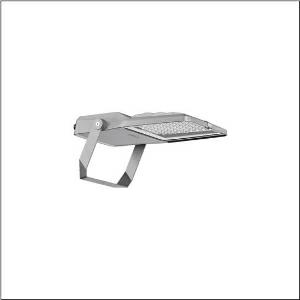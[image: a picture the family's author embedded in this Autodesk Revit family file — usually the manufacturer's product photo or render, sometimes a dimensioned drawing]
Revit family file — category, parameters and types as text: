
# Revit family: floodlight_fl_21_iq_mini___pl64_5xa7772d3e1a_da13
name_source: partatom
category: Lighting Fixtures
units: mm (PartAtom-declared; Revit-internal decimal feet)

## family parameters
Cut with Voids When Loaded = No
Host = Face
Light Source = No
Part Type = Normal
Room Calculation Point = No
Round Connector Dimension = Use Diameter
Shared = No

## types (1)
- --- (1 x LED, 14810 lm, 143 W, 3000K)
    Apparent Load = 143 VA
    CIE Flux Codes = 28 80 98 100 100
    Color Rendering = 80
    Color Temperature = 3000K
    Default Elevation = 1800 mm
    Description = Floodlight FL 21 iQ mini, floodlight, primary light control with lens, of PMMA, primary optical cover: protective disc, of toughened safety glass, transparent, light distribution: PL64, light emission: direct distribution, installation type: surface-mounted, LED, High Power LED, rated luminous flux: 14.810lm, luminous efficacy: 104lm/W, light colour: 830, colour temperature: 3000K, control gear: iQ Street-Remote/DALI, control: Street-Remote, Auto-Match, Temp-Guard, Night-Set, Smart-Wire, Desk-Remote (wireless, voltage-free reading and setting of iQ features in the workshop via application-optimized NFC function/RFID function), optimised constant luminous flux control (CLO 2.0), with terminal, 6-pole, mains connection: 220..240V, AC, 50/60Hz, start of lifetime: 143W, end of service life: 152W, reduction: 61W, luminaire housing, of diecast aluminium, powder-coated, Siteco® metallic grey (DB 702S), corrosivity category C5 mid according to DIN EN ISO 12944, suitable for swimming pools, chlorine-resistant, sealing non-destructively replaceable, mounting bracket, of steel, galvanised, powder-coated, Siteco® metallic grey (DB 702S), protection rating (complete): IP66, insulation class (complete): insulation class II (safety insulation), certification: CE, ENEC, VDE, protection symbol: D, impact resistance: IK08, permissible operating ambient temperature: -40..+40°C, permissible operating ambient temperature for outdoor applications: -40..+50°C, standard: DIN EN 12944, LABS conformity tested according to VDMA 24364:2018-05, packaging unit: 1 piece

Light Distribution: PL64
    Height = 70 mm
    Lamp = 1 x LED
    Lamp Light Flux = 14810 lm
    Lamp Power = 143 W
    Lamp count = 1
    Length = 485 mm
    Luminous efficacy = 104 lm/W
    Manufacturer = Siteco
    ModVariant = No
    Model = 5XA7772D3E1A
    Number of Poles = 1
    OnlyDefault = Yes
    Power Factor = 1
    Product Name = Floodlight FL 21 iQ mini | PL64
    Product group = floodlight | pylon annexe
    ProductGroupID = 6200
    Protection Class = Protection class II
    Protection Degree = IP 66
    RLX_Detail_Level = 1
    RLX_Emergency_Light_Flux = 0 lm
    RLX_Emergency_Type = 0
    RLX_Emergency_Type_DB = No
    RlxData = <blob elided: 96501 chars, md5=3e34074b>
    Socket = socket
    Standby Power = 0 W
    System Light Flux = 14810 lm
    System Power = 143 W
    Type Comments = factory setting: luminous flux: 100 % | dim-lin: 254 | 730 mA
    Type Image = l_1006845.jpg
    URL = http://relux.com
    VarID = @adj_165764
    Voltage = 0 V
    Weight = 0.00 kg
    Width = 337 mm

## geometry (parser evidence)
native form markers: Blend x4, Sweep x12
no freeform markers — native parametric forms only
